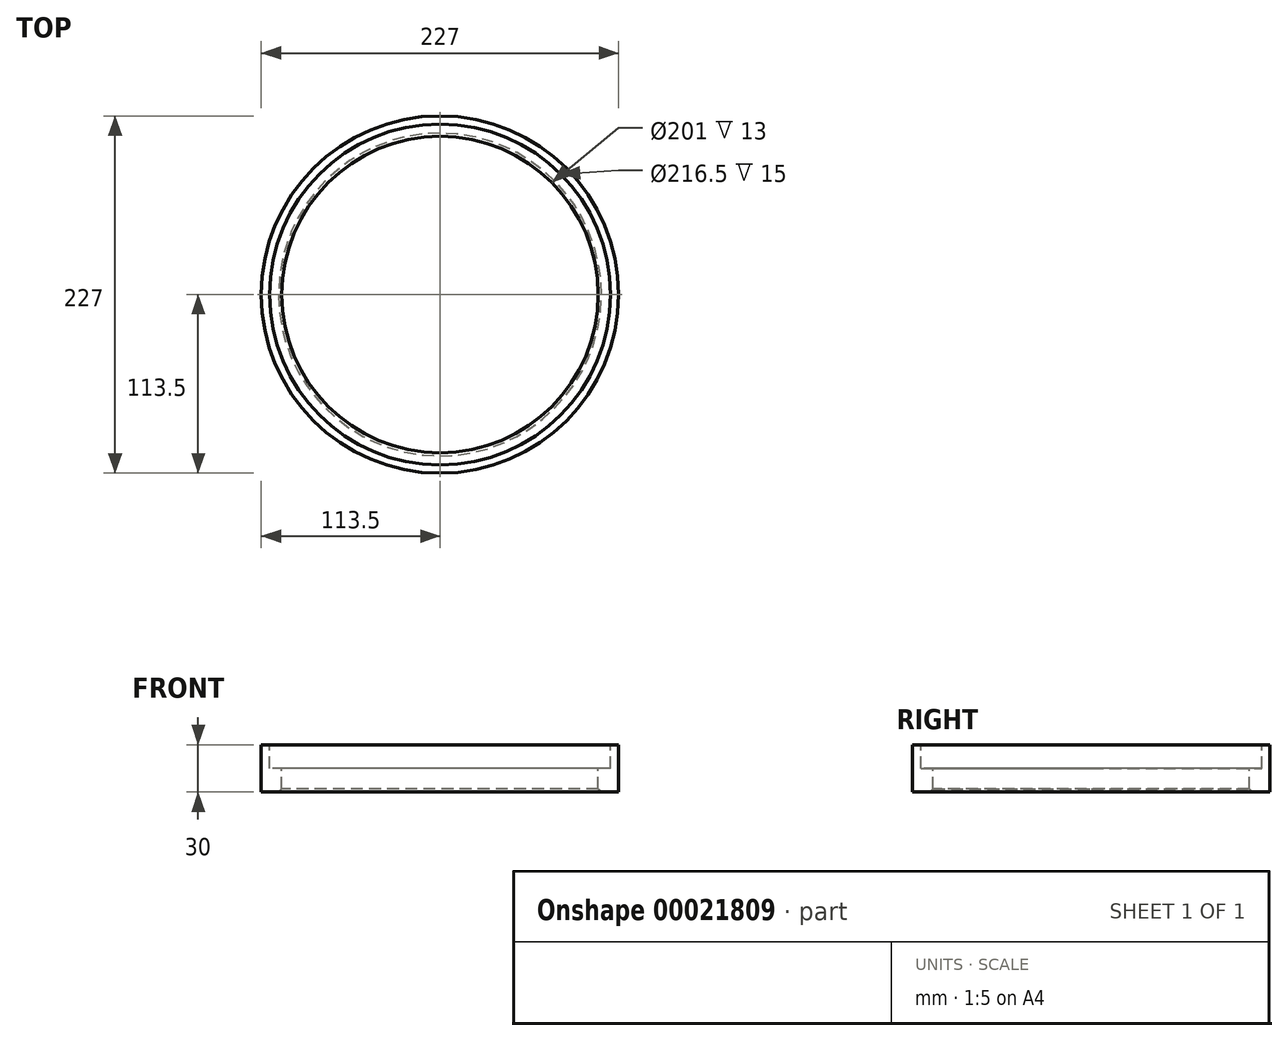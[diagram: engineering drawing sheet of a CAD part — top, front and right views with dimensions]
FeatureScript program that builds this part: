
annotation { "Feature Type Name" : "Feature", "Feature Type Description" : "" }
export const myFeature = defineFeature(function(context is Context, id is Id, definition is map)
    precondition{}
    {
        {
            var Q0;
            Q0=qCreatedBy(makeId("Front.planeOp"),FACE);
            var sketch = newSketch(context, id + "F0", { "sketchPlane" : qUnion([Q0])});
            skLineSegment(sketch, "E0", {"start": v(-113.5, 0) * mm, "end": v(-108.25, 0) * mm});
            skLineSegment(sketch, "E1", {"start": v(-108.25, 0) * mm, "end": v(-108.25, -15) * mm});
            skLineSegment(sketch, "E2", {"start": v(-108.25, -15) * mm, "end": v(-100.5, -15) * mm});
            skLineSegment(sketch, "E3", {"start": v(-100.5, -15) * mm, "end": v(-100.5, -28) * mm});
            skLineSegment(sketch, "E4", {"start": v(-102.5, -30) * mm, "end": v(-113.5, -30) * mm});
            skLineSegment(sketch, "E5", {"start": v(-113.5, -30) * mm, "end": v(-113.5, 0) * mm});
            skLineSegment(sketch, "E6", {"start": v(0, 47.06) * mm, "end": v(0, -44.28) * mm, "construction": true});
            skLineSegment(sketch, "E7", {"start": v(-100.5, -28) * mm, "end": v(-102.5, -30) * mm});
            skSolve(sketch);
        }
        {
            var Q0;
            Q0=makeQuery(id+"F0.imprint","IMPRINT",FACE,{"disambiguationData":[TD([[makeQuery(id+"F0.imprint","IMPRINT",EDGE,{"derivedFrom":sQuery(id+"F0.wireOp",EDGE,"E0")}),-1.0]])]});
            var Q1;
            Q1=sQuery(id+"F0.wireOp",EDGE,"E6");
            revolve(context, id + "F1", {"entities" : qUnion([Q0]), "axis" : qUnion([Q1]), "revolveType" : RevolveType.FULL});
        }
    });
